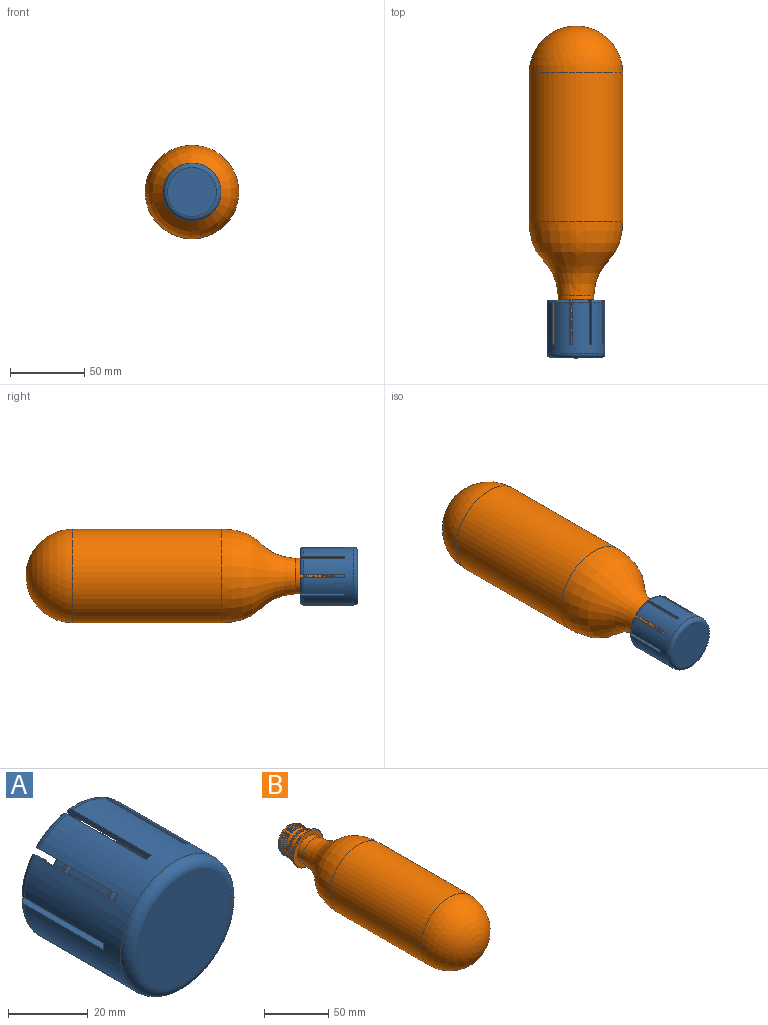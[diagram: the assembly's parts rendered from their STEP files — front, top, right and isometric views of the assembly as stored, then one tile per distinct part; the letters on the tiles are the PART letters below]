
ASSEMBLY  parts=2 mates=1
PART A: 105 faces, bbox 42.3x39.1x42.3 mm
  f0: cylinder r=17.5mm len=35mm, axis (0,-1,0), area 2702.5mm2, adj f1,f2,f3,f4,f5,f6,f7,f8
  f1: cone r=17.5mm half-angle=45deg, axis (0,-1,0), area 14mm2, adj f0,f10,f92,f103
  f2: cone r=17.5mm half-angle=45deg, axis (0,-1,0), area 14mm2, adj f0,f11,f95,f100
  f3: cone r=17.5mm half-angle=45deg, axis (0,-1,0), area 14mm2, adj f0,f12,f97,f101
  f4: cone r=17.5mm half-angle=45deg, axis (0,-1,0), area 14mm2, adj f0,f13,f80,f94
  f5: cone r=17.5mm half-angle=45deg, axis (0,-1,0), area 14mm2, adj f0,f14,f89,f91
  f6: cone r=17.5mm half-angle=45deg, axis (0,-1,0), area 14mm2, adj f0,f15,f86,f88
  f7: cone r=17.5mm half-angle=45deg, axis (0,-1,0), area 14mm2, adj f0,f16,f83,f85
  f8: cone r=17.5mm half-angle=45deg, axis (0,-1,0), area 14mm2, adj f0,f17,f82,f98
  f9: cone r=17.5mm half-angle=45deg, axis (0,-1,0), area 14mm2, adj f0,f18,f79,f104
  f10: plane 7.88x7.04mm, normal (0,-1,0), area 17.6mm2, adj f1,f19,f92,f103
  f11: plane 9.24x3.47mm, normal (0,-1,0), area 17.6mm2, adj f2,f20,f95,f100
  f12: plane 8.48x5.98mm, normal (0,-1,0), area 17.6mm2, adj f3,f21,f97,f101
  f13: plane 7.88x7.04mm, normal (0,-1,0), area 17.6mm2, adj f4,f22,f80,f94
  f14: plane 9.24x3.47mm, normal (0,-1,0), area 17.6mm2, adj f5,f23,f89,f91
  f15: plane 8.48x5.98mm, normal (0,-1,0), area 17.6mm2, adj f6,f24,f86,f88
  f16: plane 8.82x4.75mm, normal (0,-1,0), area 17.6mm2, adj f7,f25,f83,f85
  f17: plane 8.82x4.75mm, normal (0,-1,0), area 17.6mm2, adj f8,f26,f82,f98
  f18: plane 9.39x2.57mm, normal (0,-1,0), area 17.6mm2, adj f9,f27,f79,f104
  f19: cylinder r=14.5mm len=6.14mm, axis (0,-1,0), area 8.1mm2, adj f10,f28,f92,f103
  f20: cylinder r=14.5mm len=7.89mm, axis (0,-1,0), area 8.1mm2, adj f11,f29,f95,f100
  f21: cylinder r=14.5mm len=6.94mm, axis (0,-1,0), area 8.1mm2, adj f12,f30,f97,f101
  f22: cylinder r=14.5mm len=6.14mm, axis (0,-1,0), area 8.1mm2, adj f13,f31,f80,f94
  f23: cylinder r=14.5mm len=7.89mm, axis (0,-1,0), area 8.1mm2, adj f14,f32,f89,f91
  f24: cylinder r=14.5mm len=6.94mm, axis (0,-1,0), area 8.1mm2, adj f15,f33,f86,f88
  f25: cylinder r=14.5mm len=7.53mm, axis (0,-1,0), area 8.1mm2, adj f16,f34,f83,f85
  f26: cylinder r=14.5mm len=7.53mm, axis (0,-1,0), area 8.1mm2, adj f17,f35,f82,f98
  f27: cylinder r=14.5mm len=8.02mm, axis (0,-1,0), area 8.1mm2, adj f18,f36,f79,f104
  f28: cone r=14.5mm half-angle=45deg, axis (0,1,0), area 12mm2, adj f19,f37,f92,f103
  f29: cone r=14.5mm half-angle=45deg, axis (0,1,0), area 12mm2, adj f20,f38,f95,f100
  f30: cone r=14.5mm half-angle=45deg, axis (0,1,0), area 12mm2, adj f21,f39,f97,f101
  f31: cone r=14.5mm half-angle=45deg, axis (0,1,0), area 12mm2, adj f22,f40,f80,f94
  f32: cone r=14.5mm half-angle=45deg, axis (0,1,0), area 12mm2, adj f23,f41,f89,f91
  f33: cone r=14.5mm half-angle=45deg, axis (0,1,0), area 12mm2, adj f24,f42,f86,f88
  f34: cone r=14.5mm half-angle=45deg, axis (0,1,0), area 12mm2, adj f25,f43,f83,f85
  f35: cone r=14.5mm half-angle=45deg, axis (0,1,0), area 12mm2, adj f26,f44,f82,f98
  f36: cone r=14.5mm half-angle=45deg, axis (0,1,0), area 12mm2, adj f27,f45,f79,f104
  f37: plane 8.4x7.48mm, normal (0,1,0), area 19mm2, adj f28,f47,f92,f103
  f38: plane 9.92x3.6mm, normal (0,1,0), area 19mm2, adj f29,f48,f95,f100
  f39: plane 9.07x6.32mm, normal (0,1,0), area 19mm2, adj f30,f49,f97,f101
  f40: plane 8.4x7.48mm, normal (0,1,0), area 19mm2, adj f31,f50,f80,f94
  f41: plane 9.92x3.6mm, normal (0,1,0), area 19mm2, adj f32,f51,f89,f91
  f42: plane 9.07x6.32mm, normal (0,1,0), area 19mm2, adj f33,f52,f86,f88
  f43: plane 9.46x4.98mm, normal (0,1,0), area 19mm2, adj f34,f53,f83,f85
  f44: plane 9.46x4.98mm, normal (0,1,0), area 19mm2, adj f35,f54,f82,f98
  f45: plane 10.07x2.62mm, normal (0,1,0), area 19mm2, adj f36,f55,f79,f104
  f46: cylinder r=19.5mm len=39mm, axis (0,-1,0), area 3661.5mm2, adj f47,f48,f49,f50,f51,f52,f53,f54
  f47: torus R=17.5mm, axis (0,-1,0), area 34.8mm2, adj f37,f46,f92,f103
  f48: torus R=17.5mm, axis (0,-1,0), area 34.8mm2, adj f38,f46,f95,f100
  f49: torus R=17.5mm, axis (0,-1,0), area 34.8mm2, adj f39,f46,f97,f101
  f50: torus R=17.5mm, axis (0,-1,0), area 34.8mm2, adj f40,f46,f80,f94
  f51: torus R=17.5mm, axis (0,-1,0), area 34.8mm2, adj f41,f46,f89,f91
  f52: torus R=17.5mm, axis (0,-1,0), area 34.8mm2, adj f42,f46,f86,f88
  f53: torus R=17.5mm, axis (0,-1,0), area 34.8mm2, adj f43,f46,f83,f85
  f54: torus R=17.5mm, axis (0,-1,0), area 34.8mm2, adj f44,f46,f82,f98
  f55: torus R=17.5mm, axis (0,-1,0), area 34.8mm2, adj f45,f46,f79,f104
  f56: cylinder r=10.5mm len=21mm, axis (0,-1,0), area 712.5mm2, adj f58,f69
  f57: plane 33x33mm, normal (0,-1,0), area 855.3mm2, adj f76
  f58: plane 31x31mm, normal (0,1,0), area 408.4mm2, adj f56,f77
  f59: plane 20.6x20.6mm, normal (0,-1,0), area 34.6mm2, adj f61,f70
  f60: plane 20.6x20.6mm, normal (0,1,0), area 34.6mm2, adj f61,f69
  f61: torus R=9.75mm, axis (0,-1,0), area 179.9mm2, adj f59,f60
  f62: cylinder r=10.5mm len=21mm, axis (0,-1,0), area 897.2mm2, adj f70,f71
  f63: plane 20.6x20.6mm, normal (0,1,0), area 34.6mm2, adj f65,f71
  f64: plane 20.6x20.6mm, normal (0,-1,0), area 34.6mm2, adj f65,f72
  f65: torus R=9.75mm, axis (0,-1,0), area 179.9mm2, adj f63,f64
  f66: plane 19x19mm, normal (0,1,0), area 129.6mm2, adj f67,f73
  f67: cone r=9.5mm half-angle=45deg, axis (0,-1,0), area 88.9mm2, adj f66,f68
  f68: cylinder r=10.5mm len=21mm, axis (0,-1,0), area 184.7mm2, adj f67,f72
  f69: cone r=10.5mm half-angle=45deg, axis (0,-1,0), area 18.5mm2, adj f56,f60
  f70: cone r=10.5mm half-angle=45deg, axis (0,1,0), area 18.5mm2, adj f59,f62
  f71: cone r=10.3mm half-angle=45deg, axis (0,-1,0), area 18.5mm2, adj f62,f63
  f72: cone r=10.3mm half-angle=45deg, axis (0,1,0), area 18.5mm2, adj f64,f68
  f73: cylinder r=7mm len=25mm, axis (0,1,0), area 1099.6mm2, adj f66,f75
  f74: plane 4x4mm, normal (0,1,0), area 12.6mm2, adj f75
  f75: torus R=2mm, axis (0,1,0), area 255.8mm2, adj f73,f74
  f76: torus R=16.5mm, axis (0,1,0), area 545.1mm2, adj f46,f57
  f77: torus R=15.5mm, axis (0,-1,0), area 331.1mm2, adj f0,f58
  f78: plane 2.57x2.56mm, normal (0,1,0), area 4mm2, adj f0,f46,f79,f80
  f79: plane 30.05x4.76mm, normal (-0.34,0,0.94), area 65.2mm2, adj f0,f9,f18,f27,f36,f45,f46,f55
  f80: plane 30.05x4.76mm, normal (0.34,0,-0.94), area 65.2mm2, adj f0,f4,f13,f22,f31,f40,f46,f50
  f81: plane 2.03x2mm, normal (0,1,0), area 4mm2, adj f0,f46,f82,f83
  f82: plane 30.05x5.06mm, normal (0,0,-1), area 65.2mm2, adj f0,f8,f17,f26,f35,f44,f46,f54
  f83: plane 30.05x5.06mm, normal (0,0,1), area 65.2mm2, adj f0,f7,f16,f25,f34,f43,f46,f53
  f84: plane 2.82x2.82mm, normal (0,1,0), area 4mm2, adj f0,f46,f85,f86
  f85: plane 30.05x3.89mm, normal (0.64,0,-0.77), area 65.2mm2, adj f0,f7,f16,f25,f34,f43,f46,f53
  f86: plane 30.05x3.89mm, normal (-0.64,0,0.77), area 65.2mm2, adj f0,f6,f15,f24,f33,f42,f46,f52
  f87: plane 2.32x2.32mm, normal (0,1,0), area 4mm2, adj f0,f46,f88,f89
  f88: plane 30.05x4.98mm, normal (0.98,0,-0.17), area 65.2mm2, adj f0,f6,f15,f24,f33,f42,f46,f52
  f89: plane 30.05x4.98mm, normal (-0.98,0,0.17), area 65.2mm2, adj f0,f5,f14,f23,f32,f41,f46,f51
  f90: plane 2.73x2.73mm, normal (0,1,0), area 4mm2, adj f0,f46,f91,f92
  f91: plane 30.05x4.39mm, normal (0.87,0,0.5), area 65.2mm2, adj f0,f5,f14,f23,f32,f41,f46,f51
  f92: plane 30.05x4.39mm, normal (-0.87,0,-0.5), area 65.2mm2, adj f0,f1,f10,f19,f28,f37,f46,f47
  f93: plane 2.73x2.73mm, normal (0,1,0), area 4mm2, adj f0,f46,f94,f95
  f94: plane 30.05x4.39mm, normal (-0.87,0,0.5), area 65.2mm2, adj f0,f4,f13,f22,f31,f40,f46,f50
  f95: plane 30.05x4.39mm, normal (0.87,0,-0.5), area 65.2mm2, adj f0,f2,f11,f20,f29,f38,f46,f48
  f96: plane 2.82x2.82mm, normal (0,1,0), area 4mm2, adj f0,f46,f97,f98
  f97: plane 30.05x3.89mm, normal (-0.64,0,-0.77), area 65.2mm2, adj f0,f3,f12,f21,f30,f39,f46,f49
  f98: plane 30.05x3.89mm, normal (0.64,0,0.77), area 65.2mm2, adj f0,f8,f17,f26,f35,f44,f46,f54
  f99: plane 2.32x2.32mm, normal (0,1,0), area 4mm2, adj f0,f46,f100,f101
  f100: plane 30.05x4.98mm, normal (-0.98,0,-0.17), area 65.2mm2, adj f0,f2,f11,f20,f29,f38,f46,f48
  f101: plane 30.05x4.98mm, normal (0.98,0,0.17), area 65.2mm2, adj f0,f3,f12,f21,f30,f39,f46,f49
  f102: plane 2.57x2.56mm, normal (0,1,0), area 4mm2, adj f0,f46,f103,f104
  f103: plane 30.05x4.76mm, normal (0.34,0,0.94), area 65.2mm2, adj f0,f1,f10,f19,f28,f37,f46,f47
  f104: plane 30.05x4.76mm, normal (-0.34,0,-0.94), area 65.2mm2, adj f0,f9,f18,f27,f36,f45,f46,f55
PART B: 323 faces, bbox 63x207.7x63 mm
  f0: plane 22x22mm, normal (0,-1,0), area 16.1mm2, adj f284,f322
  f1: cylinder r=12.26mm len=24.51mm, axis (0,1,0), area 270.6mm2, adj f14,f199,f200,f215,f216,f217,f218,f219
  f2: bspline ~17.68x9.49mm, area 6.4mm2, adj f3,f24,f177,f207
  f3: bspline ~1.8x1.33mm, area 0.7mm2, adj f2,f29,f30,f208,f209,f293
  f4: cylinder r=16.5mm len=33mm, axis (0,-1,0), area 65.2mm2, adj f9,f17
  f5: plane 32.2x32.2mm, normal (0,-1,0), area 361.9mm2, adj f17,f318
  f6: torus R=14.36mm, axis (0,-1,0), area 154.3mm2, adj f7,f8
  f7: cone r=16.5mm half-angle=71deg, axis (0,-1,0), area 219mm2, adj f6,f9
  f8: cylinder r=12.86mm len=25.71mm, axis (0,-1,0), area 233.4mm2, adj f6,f15
  f9: torus R=15.86mm, axis (0,1,0), area 81.5mm2, adj f4,f7
  f10: cylinder r=13.98mm len=27.97mm, axis (0,-1,0), area 21.9mm2, adj f13,f16
  f11: plane 27.17x27.17mm, normal (0,-1,0), area 27.8mm2, adj f12,f15
  f12: cone r=13.98mm half-angle=89.5deg, axis (0,1,0), area 13.1mm2, adj f11,f16
  f13: torus R=12.19mm, axis (0,1,0), area 188.6mm2, adj f10,f14
  f14: torus R=13.06mm, axis (0,1,0), area 76.9mm2, adj f1,f13
  f15: torus R=13.25mm, axis (0,1,0), area 51.3mm2, adj f8,f11
  f16: torus R=13.74mm, axis (0,-1,0), area 34.1mm2, adj f10,f12
  f17: torus R=16.1mm, axis (0,1,0), area 64.6mm2, adj f4,f5
  f18: plane 23.78x23.78mm, normal (0,1,0), area 52.2mm2, adj f19,f285
  f19: torus R=11.89mm, axis (0,1,0), area 70.2mm2, adj f18,f20
  f20: cylinder r=12.47mm len=24.94mm, axis (0,1,0), area 32.9mm2, adj f19,f21
  f21: plane 25.07x25.07mm, normal (0,1,0), area 5.1mm2, adj f20,f22
  f22: cylinder r=12.54mm len=25.07mm, axis (0,1,0), area 26.9mm2, adj f21,f178,f197,f198,f201,f202,f204,f205
  f23: bspline ~24.84x8.59mm, area 3.5mm2, adj f24,f26,f31,f191
  f24: bspline ~22.43x6.24mm, area 14.9mm2, adj f2,f23,f30,f176,f192,f195
  f25: bspline ~25.64x9.84mm, area 19.2mm2, adj f26,f33,f189,f299
  f26: bspline ~22.43x6.19mm, area 18.9mm2, adj f23,f25,f32,f190
  f27: plane 0.82x0.55mm, normal (-0.56,0,-0.83), area 0.3mm2, adj f189,f190,f191,f196,f298
  f28: plane 10.27x4.99mm, normal (0,1,0), area 4.5mm2, adj f176,f177,f196,f205
  f29: plane 0.71x0.67mm, normal (-0.56,0,0.83), area 0.3mm2, adj f3,f31,f33,f295
  f30: sphere r=0.64mm, area 0.6mm2, adj f3,f24,f31
  f31: bspline ~0.77x0.5mm, area 0.1mm2, adj f23,f29,f30,f32
  f32: sphere r=0.64mm, area 0.4mm2, adj f26,f31,f33
  f33: bspline ~2.32x1.7mm, area 0.8mm2, adj f25,f29,f32,f297
  f34: bspline ~12.87x9.55mm, area 7.6mm2, adj f36,f38,f45,f231
  f35: bspline ~12.01x6.95mm, area 1.7mm2, adj f36,f39,f41,f47
  f36: bspline ~11.69x5.81mm, area 9.4mm2, adj f34,f35,f43,f46
  f37: bspline ~12.81x9.65mm, area 7.6mm2, adj f40,f41,f49,f239
  f38: bspline ~5.65x4.41mm, area 1.2mm2, adj f34,f43,f232
  f39: bspline ~6.34x4.79mm, area 0.8mm2, adj f35,f42,f43,f236
  f40: bspline ~5.7x4.31mm, area 1.2mm2, adj f37,f42,f240
  f41: bspline ~11.67x5.85mm, area 9.4mm2, adj f35,f37,f42,f48
  f42: bspline ~6.09x3.8mm, area 3.8mm2, adj f39,f40,f41,f238
  f43: bspline ~5.63x3.35mm, area 3.7mm2, adj f36,f38,f39,f234
  f44: plane 0.6x0.54mm, normal (-0.56,0,-0.83), area 0.2mm2, adj f45,f47,f49,f235
  f45: bspline ~2.31x1.7mm, area 0.7mm2, adj f34,f44,f46,f233
  f46: sphere r=0.64mm, area 0.4mm2, adj f36,f45,f47
  f47: bspline ~0.76x0.72mm, area 0.1mm2, adj f35,f44,f46,f48
  f48: sphere r=0.64mm, area 0.3mm2, adj f41,f47,f49
  f49: bspline ~2.3x1.67mm, area 0.6mm2, adj f37,f44,f48,f237
  f50: plane 0.6x0.54mm, normal (-0.56,0,-0.83), area 0.2mm2, adj f57,f59,f61,f225
  f51: bspline ~22.41x6.3mm, area 18.7mm2, adj f54,f55,f58,f65
  f52: bspline ~22.41x6.34mm, area 18.7mm2, adj f53,f55,f60,f63
  f53: bspline ~24.86x8.99mm, area 15.2mm2, adj f52,f61,f62,f229
  f54: bspline ~24.86x8.89mm, area 15.2mm2, adj f51,f57,f66,f224
  f55: bspline ~24.87x7.99mm, area 3.5mm2, adj f51,f52,f59,f64
  f56: plane 0.6x0.54mm, normal (-0.56,0,0.83), area 0.2mm2, adj f62,f64,f66,f228
  f57: bspline ~2.31x1.7mm, area 0.7mm2, adj f50,f54,f58,f223
  f58: sphere r=0.64mm, area 0.4mm2, adj f51,f57,f59
  f59: bspline ~0.76x0.72mm, area 0.1mm2, adj f50,f55,f58,f60
  f60: sphere r=0.64mm, area 0.4mm2, adj f52,f59,f61
  f61: bspline ~2.3x1.67mm, area 0.6mm2, adj f50,f53,f60,f227
  f62: bspline ~2.32x1.7mm, area 0.7mm2, adj f53,f56,f63,f230
  f63: sphere r=0.64mm, area 0.5mm2, adj f52,f62,f64
  f64: bspline ~0.76x0.72mm, area 0.1mm2, adj f55,f56,f63,f65
  f65: sphere r=0.64mm, area 0.4mm2, adj f51,f64,f66
  f66: bspline ~2.29x1.66mm, area 0.6mm2, adj f54,f56,f65,f226
  f67: bspline ~11.24x1.74mm, area 6.6mm2, adj f68,f70,f77,f82
  f68: bspline ~13.15x4.07mm, area 5.5mm2, adj f67,f78,f83,f217
  f69: bspline ~11.24x1.71mm, area 6.6mm2, adj f70,f71,f75,f80
  f70: bspline ~11.38x1.47mm, area 1.2mm2, adj f67,f69,f76,f81
  f71: bspline ~13.15x4.01mm, area 5.5mm2, adj f69,f74,f79,f220
  f72: plane 0.74x0.65mm, normal (1,0,-0.03), area 0.3mm2, adj f74,f76,f78,f221
  f73: plane 0.74x0.65mm, normal (-1,0,-0.03), area 0.3mm2, adj f79,f81,f83,f216
  f74: bspline ~2.37x1.32mm, area 0.7mm2, adj f71,f72,f75,f222
  f75: sphere r=0.64mm, area 0.3mm2, adj f69,f74,f76
  f76: bspline ~0.59x0.5mm, area 0.1mm2, adj f70,f72,f75,f77
  f77: sphere r=0.64mm, area 0.4mm2, adj f67,f76,f78
  f78: bspline ~2.37x1.37mm, area 0.7mm2, adj f68,f72,f77,f219
  f79: bspline ~2.37x1.37mm, area 0.7mm2, adj f71,f73,f80,f218
  f80: sphere r=0.64mm, area 0.3mm2, adj f69,f79,f81
  f81: bspline ~0.59x0.5mm, area 0.1mm2, adj f70,f73,f80,f82
  f82: sphere r=0.64mm, area 0.3mm2, adj f67,f81,f83
  f83: bspline ~2.37x1.32mm, area 0.7mm2, adj f68,f73,f82,f215
  f84: bspline ~5.66x3.22mm, area 3.2mm2, adj f85,f86,f179,f305
  f85: bspline ~4.56x3.56mm, area 1.6mm2, adj f84,f87,f306
  f86: bspline ~6.72x1.64mm, area 3.5mm2, adj f84,f87,f89,f180,f184
  f87: bspline ~6.62x3.63mm, area 3.7mm2, adj f85,f86,f182,f307
  f88: plane 7.97x1.4mm, normal (0,1,0), area 4.7mm2, adj f179,f180,f181,f188,f212
  f89: bspline ~6.63x1.64mm, area 0.3mm2, adj f86,f181,f183,f185
  f90: plane 1x0.38mm, normal (1,0,-0.03), area 0.2mm2, adj f182,f184,f188,f309
  f91: plane 0.6x0.54mm, normal (0.56,0,-0.83), area 0.2mm2, adj f98,f100,f102,f254
  f92: bspline ~22.64x6.84mm, area 18.7mm2, adj f95,f96,f99,f104
  f93: bspline ~22.64x6.79mm, area 18.7mm2, adj f94,f96,f101,f106
  f94: bspline ~24.84x9.32mm, area 15.2mm2, adj f93,f102,f107,f255
  f95: bspline ~24.84x9.22mm, area 15.2mm2, adj f92,f98,f103,f250
  f96: bspline ~24.86x8.39mm, area 3.5mm2, adj f92,f93,f100,f105
  f97: plane 0.6x0.54mm, normal (0.56,0,0.83), area 0.2mm2, adj f103,f105,f107,f251
  f98: bspline ~2.29x1.66mm, area 0.6mm2, adj f91,f95,f99,f252
  f99: sphere r=0.64mm, area 0.6mm2, adj f92,f98,f100
  f100: bspline ~0.76x0.5mm, area 0.1mm2, adj f91,f96,f99,f101
  f101: sphere r=0.64mm, area 0.5mm2, adj f93,f100,f102
  f102: bspline ~1.83x1.37mm, area 0.7mm2, adj f91,f94,f101,f256
  f103: bspline ~2.31x1.7mm, area 0.7mm2, adj f95,f97,f104,f249
  f104: sphere r=0.64mm, area 0.5mm2, adj f92,f103,f105
  f105: bspline ~0.76x0.5mm, area 0.1mm2, adj f96,f97,f104,f106
  f106: sphere r=0.64mm, area 0.4mm2, adj f93,f105,f107
  f107: bspline ~2.3x1.67mm, area 0.6mm2, adj f94,f97,f106,f253
  f108: plane 0.6x0.54mm, normal (0.56,0,-0.83), area 0.2mm2, adj f115,f117,f119,f270
  f109: bspline ~22.43x6.07mm, area 18.7mm2, adj f112,f113,f116,f121
  f110: bspline ~22.43x6.11mm, area 18.7mm2, adj f111,f113,f118,f123
  f111: bspline ~25.34x9.39mm, area 15.2mm2, adj f110,f119,f124,f271
  f112: bspline ~25.34x9.28mm, area 15.2mm2, adj f109,f115,f120,f266
  f113: bspline ~25.36x8.47mm, area 3.5mm2, adj f109,f110,f117,f122
  f114: plane 0.6x0.54mm, normal (0.56,0,0.83), area 0.2mm2, adj f120,f122,f124,f267
  f115: bspline ~2.29x1.66mm, area 0.6mm2, adj f108,f112,f116,f268
  f116: sphere r=0.64mm, area 0.6mm2, adj f109,f115,f117
  f117: bspline ~0.76x0.5mm, area 0.1mm2, adj f108,f113,f116,f118
  f118: sphere r=0.64mm, area 0.5mm2, adj f110,f117,f119
  f119: bspline ~2.32x1.7mm, area 0.7mm2, adj f108,f111,f118,f272
  f120: bspline ~2.31x1.7mm, area 0.7mm2, adj f112,f114,f121,f265
  f121: sphere r=0.64mm, area 0.4mm2, adj f109,f120,f122
  f122: bspline ~0.76x0.72mm, area 0.1mm2, adj f113,f114,f121,f123
  f123: sphere r=0.64mm, area 0.4mm2, adj f110,f122,f124
  f124: bspline ~2.3x1.67mm, area 0.6mm2, adj f111,f114,f123,f269
  f125: bspline ~13.2x1.99mm, area 1.2mm2, adj f127,f129,f134,f139
  f126: bspline ~13.16x3.98mm, area 5.5mm2, adj f127,f132,f137,f258
  f127: bspline ~9.82x1.35mm, area 6.6mm2, adj f125,f126,f133,f138
  f128: bspline ~13.16x3.92mm, area 5.5mm2, adj f129,f136,f141,f263
  f129: bspline ~9.82x1.32mm, area 6.6mm2, adj f125,f128,f135,f140
  f130: plane 0.74x0.65mm, normal (1,0,0.03), area 0.3mm2, adj f137,f139,f141,f259
  f131: plane 0.74x0.65mm, normal (-1,0,0.03), area 0.3mm2, adj f132,f134,f136,f262
  f132: bspline ~2.37x1.32mm, area 0.7mm2, adj f126,f131,f133,f260
  f133: sphere r=0.64mm, area 0.3mm2, adj f127,f132,f134
  f134: bspline ~0.59x0.5mm, area 0.1mm2, adj f125,f131,f133,f135
  f135: sphere r=0.64mm, area 0.3mm2, adj f129,f134,f136
  f136: bspline ~2.37x1.37mm, area 0.7mm2, adj f128,f131,f135,f264
  f137: bspline ~2.37x1.37mm, area 0.7mm2, adj f126,f130,f138,f257
  f138: sphere r=0.64mm, area 0.4mm2, adj f127,f137,f139
  f139: bspline ~0.59x0.5mm, area 0.1mm2, adj f125,f130,f138,f140
  f140: sphere r=0.64mm, area 0.3mm2, adj f129,f139,f141
  f141: bspline ~2.37x1.32mm, area 0.7mm2, adj f128,f130,f140,f261
  f142: plane 0.74x0.65mm, normal (1,0,0.03), area 0.3mm2, adj f154,f156,f158,f277
  f143: bspline ~14.75x4.27mm, area 5.9mm2, adj f147,f149,f154,f274,f276
  f144: bspline ~14.75x4.21mm, area 5.5mm2, adj f146,f153,f158,f281
  f145: bspline ~14.78x2.33mm, area 1.2mm2, adj f146,f147,f151,f156
  f146: bspline ~11.25x1.67mm, area 6.6mm2, adj f144,f145,f152,f157
  f147: bspline ~11.25x1.69mm, area 6.6mm2, adj f143,f145,f150,f155
  f148: plane 0.74x0.65mm, normal (-1,0,0.03), area 0.3mm2, adj f149,f151,f153,f280
  f149: bspline ~2.37x1.32mm, area 0.7mm2, adj f143,f148,f150,f278
  f150: sphere r=0.64mm, area 0.3mm2, adj f147,f149,f151
  f151: bspline ~0.59x0.5mm, area 0.1mm2, adj f145,f148,f150,f152
  f152: sphere r=0.64mm, area 0.3mm2, adj f146,f151,f153
  f153: bspline ~2.37x1.37mm, area 0.7mm2, adj f144,f148,f152,f282
  f154: bspline ~2.37x1.37mm, area 0.8mm2, adj f142,f143,f155,f273,f275
  f155: sphere r=0.64mm, area 0.4mm2, adj f147,f154,f156
  f156: bspline ~0.59x0.5mm, area 0.1mm2, adj f142,f145,f155,f157
  f157: sphere r=0.64mm, area 0.3mm2, adj f146,f156,f158
  f158: bspline ~2.37x1.32mm, area 0.7mm2, adj f142,f144,f157,f279
  f159: bspline ~11.22x1.98mm, area 6.6mm2, adj f160,f162,f169,f174
  f160: bspline ~13.17x3.73mm, area 5.5mm2, adj f159,f170,f175,f247
  f161: bspline ~11.22x1.95mm, area 6.6mm2, adj f162,f163,f167,f172
  f162: bspline ~13.21x1.76mm, area 1.2mm2, adj f159,f161,f168,f173
  f163: bspline ~13.17x3.78mm, area 5.5mm2, adj f161,f166,f171,f242
  f164: plane 0.74x0.65mm, normal (1,0,-0.03), area 0.3mm2, adj f166,f168,f170,f246
  f165: plane 0.74x0.65mm, normal (-1,0,-0.03), area 0.3mm2, adj f171,f173,f175,f243
  f166: bspline ~2.37x1.32mm, area 0.7mm2, adj f163,f164,f167,f244
  f167: sphere r=0.64mm, area 0.3mm2, adj f161,f166,f168
  f168: bspline ~0.59x0.5mm, area 0.1mm2, adj f162,f164,f167,f169
  f169: sphere r=0.64mm, area 0.4mm2, adj f159,f168,f170
  f170: bspline ~2.37x1.37mm, area 0.7mm2, adj f160,f164,f169,f248
  f171: bspline ~2.37x1.37mm, area 0.7mm2, adj f163,f165,f172,f241
  f172: sphere r=0.64mm, area 0.3mm2, adj f161,f171,f173
  f173: bspline ~0.59x0.5mm, area 0.1mm2, adj f162,f165,f172,f174
  f174: sphere r=0.64mm, area 0.3mm2, adj f159,f173,f175
  f175: bspline ~2.37x1.32mm, area 0.7mm2, adj f160,f165,f174,f245
  f176: bspline ~8.35x4.97mm, area 2.3mm2, adj f24,f28,f177,f195
  f177: bspline ~8.74x0.85mm, area 0.3mm2, adj f2,f28,f176,f206
  f178: cylinder r=0.4mm len=0.96mm, axis (0,1,0), area 0.1mm2, adj f22,f209,f286,f289
  f179: bspline ~6.37x3.38mm, area 0.9mm2, adj f84,f88,f180,f213,f214,f302,f303,f304
  f180: bspline ~1.62x0.19mm, area 0.1mm2, adj f86,f88,f179,f181
  f181: bspline ~4.5x0.97mm, area 0.6mm2, adj f88,f89,f180,f185
  f182: bspline ~2.28x1.14mm, area 0.5mm2, adj f87,f90,f184,f308
  f183: bspline ~0.37x0.27mm, area 0mm2, adj f89,f184,f186
  f184: bspline ~0.75x0.55mm, area 0.3mm2, adj f86,f90,f182,f183,f187
  f185: bspline ~0.27x0.16mm, area 0mm2, adj f89,f181,f186,f188
  f186: bspline ~0.29x0.28mm, area 0mm2, adj f183,f185,f187,f188
  f187: bspline ~0.34x0.28mm, area 0mm2, adj f184,f186,f188
  f188: cylinder r=0.4mm len=1.4mm, axis (-0.03,0,-1), area 0.6mm2, adj f88,f90,f185,f186,f187,f210,f211,f310
  f189: bspline ~2.1x1.49mm, area 0.5mm2, adj f25,f27,f190,f300
  f190: bspline ~0.67x0.66mm, area 0.3mm2, adj f26,f27,f189,f191
  f191: bspline ~0.5x0.47mm, area 0mm2, adj f23,f27,f190,f192,f193
  f192: bspline ~0.48x0.22mm, area 0mm2, adj f24,f191,f194
  f193: bspline ~0.45x0.37mm, area 0mm2, adj f191,f194,f196
  f194: bspline ~0.33x0.29mm, area 0mm2, adj f192,f193,f195,f196
  f195: bspline ~0.33x0.3mm, area 0mm2, adj f24,f176,f194,f196
  f196: cylinder r=0.4mm len=1.17mm, axis (-0.83,0,0.56), area 0.5mm2, adj f27,f28,f193,f194,f195,f203,f204,f292
  f197: cylinder r=0.4mm len=0.08mm, axis (0,1,0), area 0mm2, adj f22,f210,f314
  f198: cylinder r=0.4mm len=0.04mm, axis (0,1,0), area 0mm2, adj f22,f203,f288
  f199: torus R=12.65mm, axis (0,1,0), area 14mm2, adj f1,f201,f273,f274,f287,f303
  f200: torus R=12.65mm, axis (0,1,0), area 0.8mm2, adj f1,f202,f294,f311
  f201: torus R=12.13mm, axis (0,-1,0), area 14.6mm2, adj f22,f199,f286,f301,f302
  f202: torus R=12.13mm, axis (0,-1,0), area 1mm2, adj f22,f200,f288,f292,f312,f313,f314
  f203: bspline ~0.41x0.37mm, area 0mm2, adj f196,f198,f204,f290
  f204: bspline ~0.62x0.46mm, area 0.1mm2, adj f22,f196,f203,f205
  f205: torus R=12.94mm, axis (0,1,0), area 7.1mm2, adj f22,f28,f204,f206
  f206: bspline ~2.68x0.56mm, area 1.1mm2, adj f22,f177,f205,f207
  f207: bspline ~10.43x6.12mm, area 4.6mm2, adj f2,f22,f206,f208
  f208: bspline ~0.65x0.48mm, area 0.1mm2, adj f3,f22,f207,f209
  f209: bspline ~0.74x0.71mm, area 0.2mm2, adj f3,f178,f208,f291
  f210: bspline ~0.45x0.44mm, area 0mm2, adj f188,f197,f211,f313
  f211: bspline ~0.57x0.53mm, area 0.1mm2, adj f22,f188,f210,f212
  f212: torus R=12.93mm, axis (0,1,0), area 5mm2, adj f22,f88,f211,f213
  f213: bspline ~1.31x0.93mm, area 0.2mm2, adj f22,f179,f212,f214
  f214: bspline ~0.54x0.53mm, area 0.1mm2, adj f179,f213,f301
  f215: bspline ~1.5x1.34mm, area 0.9mm2, adj f1,f83,f216,f217
  f216: cylinder r=0.64mm len=0.65mm, axis (0,1,0), area 0.5mm2, adj f1,f73,f215,f218
  f217: bspline ~9.87x1.59mm, area 6.4mm2, adj f1,f68,f215,f219
  f218: bspline ~1.5x1.43mm, area 1mm2, adj f1,f79,f216,f220
  f219: bspline ~1.5x1.43mm, area 1mm2, adj f1,f78,f217,f221
  f220: bspline ~10.86x1.62mm, area 6.4mm2, adj f1,f71,f218,f222
  f221: cylinder r=0.64mm len=0.65mm, axis (0,1,0), area 0.5mm2, adj f1,f72,f219,f222
  f222: bspline ~1.5x1.34mm, area 0.9mm2, adj f1,f74,f220,f221
  f223: bspline ~1.53x1.38mm, area 1mm2, adj f1,f57,f224,f225
  f224: bspline ~20.86x6.13mm, area 17.4mm2, adj f1,f54,f223,f226
  f225: cylinder r=0.64mm len=0.71mm, axis (0,1,0), area 0.4mm2, adj f1,f50,f223,f227
  f226: bspline ~1.53x1.34mm, area 1mm2, adj f1,f66,f224,f228
  f227: bspline ~1.53x1.34mm, area 1mm2, adj f1,f61,f225,f229
  f228: cylinder r=0.64mm len=0.71mm, axis (0,1,0), area 0.4mm2, adj f1,f56,f226,f230
  f229: bspline ~21.47x6.19mm, area 17.4mm2, adj f1,f53,f227,f230
  f230: bspline ~1.53x1.38mm, area 1mm2, adj f1,f62,f228,f229
  f231: bspline ~12.13x6.12mm, area 8.7mm2, adj f1,f34,f232,f233
  f232: bspline ~6.08x1.34mm, area 2.7mm2, adj f1,f38,f231,f234
  f233: bspline ~1.53x1.38mm, area 1mm2, adj f1,f45,f231,f235
  f234: bspline ~2.75x1.49mm, area 1.3mm2, adj f1,f43,f232,f236
  f235: cylinder r=0.64mm len=0.71mm, axis (0,1,0), area 0.4mm2, adj f1,f44,f233,f237
  f236: bspline ~0.5x0.23mm, area 0mm2, adj f1,f39,f234,f238
  f237: bspline ~1.53x1.34mm, area 1mm2, adj f1,f49,f235,f239
  f238: bspline ~3.53x1.72mm, area 1.2mm2, adj f1,f42,f236,f240
  f239: bspline ~12.08x6.19mm, area 8.7mm2, adj f1,f37,f237,f240
  f240: bspline ~6.53x1mm, area 2.7mm2, adj f1,f40,f238,f239
  f241: bspline ~1.5x1.43mm, area 1mm2, adj f1,f171,f242,f243
  f242: bspline ~10.86x1.62mm, area 6.4mm2, adj f1,f163,f241,f244
  f243: cylinder r=0.64mm len=0.65mm, axis (0,1,0), area 0.5mm2, adj f1,f165,f241,f245
  f244: bspline ~1.5x1.34mm, area 0.9mm2, adj f1,f166,f242,f246
  f245: bspline ~1.5x1.34mm, area 0.9mm2, adj f1,f175,f243,f247
  f246: cylinder r=0.64mm len=0.65mm, axis (0,1,0), area 0.5mm2, adj f1,f164,f244,f248
  f247: bspline ~10.86x1.62mm, area 6.4mm2, adj f1,f160,f245,f248
  f248: bspline ~1.5x1.43mm, area 1mm2, adj f1,f170,f246,f247
  f249: bspline ~1.53x1.38mm, area 1mm2, adj f1,f103,f250,f251
  f250: bspline ~20.86x6.13mm, area 17.4mm2, adj f1,f95,f249,f252
  f251: cylinder r=0.64mm len=0.71mm, axis (0,1,0), area 0.4mm2, adj f1,f97,f249,f253
  f252: bspline ~1.53x1.34mm, area 1mm2, adj f1,f98,f250,f254
  f253: bspline ~1.53x1.34mm, area 1mm2, adj f1,f107,f251,f255
  f254: cylinder r=0.64mm len=0.71mm, axis (0,1,0), area 0.4mm2, adj f1,f91,f252,f256
  f255: bspline ~21.47x6.19mm, area 17.4mm2, adj f1,f94,f253,f256
  f256: bspline ~1.53x1.38mm, area 1mm2, adj f1,f102,f254,f255
  f257: bspline ~1.5x1.43mm, area 1mm2, adj f1,f137,f258,f259
  f258: bspline ~10.86x1.62mm, area 6.4mm2, adj f1,f126,f257,f260
  f259: cylinder r=0.64mm len=0.65mm, axis (0,1,0), area 0.5mm2, adj f1,f130,f257,f261
  f260: bspline ~1.34x1.26mm, area 0.9mm2, adj f1,f132,f258,f262
  f261: bspline ~1.5x1.34mm, area 0.9mm2, adj f1,f141,f259,f263
  f262: cylinder r=0.64mm len=0.65mm, axis (0,1,0), area 0.5mm2, adj f1,f131,f260,f264
  f263: bspline ~10.86x1.62mm, area 6.4mm2, adj f1,f128,f261,f264
  f264: bspline ~1.5x1.43mm, area 1mm2, adj f1,f136,f262,f263
  f265: bspline ~1.53x1.38mm, area 1mm2, adj f1,f120,f266,f267
  f266: bspline ~21.46x6.19mm, area 17.4mm2, adj f1,f112,f265,f268
  f267: cylinder r=0.64mm len=0.71mm, axis (0,1,0), area 0.4mm2, adj f1,f114,f265,f269
  f268: bspline ~1.53x1.34mm, area 1mm2, adj f1,f115,f266,f270
  f269: bspline ~1.53x1.34mm, area 1mm2, adj f1,f124,f267,f271
  f270: cylinder r=0.64mm len=0.71mm, axis (0,1,0), area 0.4mm2, adj f1,f108,f268,f272
  f271: bspline ~21.46x6.19mm, area 17.4mm2, adj f1,f111,f269,f272
  f272: bspline ~1.53x1.38mm, area 1mm2, adj f1,f119,f270,f271
  f273: bspline ~0.76x0.59mm, area 0.3mm2, adj f154,f199,f274,f275
  f274: bspline ~9.89x1.52mm, area 4.6mm2, adj f143,f199,f273,f276
  f275: bspline ~1.29x0.63mm, area 0.5mm2, adj f1,f154,f273,f277
  f276: bspline ~2.79x1.32mm, area 0.6mm2, adj f1,f143,f274,f278
  f277: cylinder r=0.64mm len=0.65mm, axis (0,1,0), area 0.5mm2, adj f1,f142,f275,f279
  f278: bspline ~1.5x1.34mm, area 0.9mm2, adj f1,f149,f276,f280
  f279: bspline ~1.5x1.34mm, area 0.9mm2, adj f1,f158,f277,f281
  f280: cylinder r=0.64mm len=0.65mm, axis (0,1,0), area 0.5mm2, adj f1,f148,f278,f282
  f281: bspline ~10.86x1.62mm, area 6.4mm2, adj f1,f144,f279,f282
  f282: bspline ~1.5x1.43mm, area 1mm2, adj f1,f153,f280,f281
  f283: cylinder r=10.87mm len=21.74mm, axis (0,1,0), area 47.8mm2, adj f284,f285
  f284: cone r=10.87mm half-angle=0.3deg, axis (0,1,0), area 1372.9mm2, adj f0,f283
  f285: torus R=11.17mm, axis (0,1,0), area 32.5mm2, adj f18,f283
  f286: bspline ~0.69x0.69mm, area 0.1mm2, adj f178,f201,f287
  f287: sphere r=0.4mm, area 0.1mm2, adj f199,f286,f289
  f288: bspline ~0.24x0.21mm, area 0mm2, adj f198,f202,f290
  f289: cylinder r=0.4mm len=0.35mm, axis (0,1,0), area 0.1mm2, adj f1,f178,f287,f291
  f290: sphere r=0.4mm, area 0mm2, adj f203,f288,f292
  f291: sphere r=0.4mm, area 0mm2, adj f209,f289,f293
  f292: bspline ~1.09x0.75mm, area 0.3mm2, adj f196,f202,f290,f294
  f293: bspline ~0.64x0.49mm, area 0.1mm2, adj f1,f3,f291,f295
  f294: sphere r=0.4mm, area 0.1mm2, adj f200,f292,f296
  f295: cylinder r=0.4mm len=0.71mm, axis (0,1,0), area 0.3mm2, adj f1,f29,f293,f297
  f296: bspline ~0.47x0.36mm, area 0.1mm2, adj f1,f196,f294,f298
  f297: bspline ~1.11x1.05mm, area 0.6mm2, adj f1,f33,f295,f299
  f298: cylinder r=0.4mm len=0.51mm, axis (0,1,0), area 0.2mm2, adj f1,f27,f296,f300
  f299: bspline ~21.37x6.25mm, area 11mm2, adj f1,f25,f297,f300
  f300: bspline ~0.85x0.8mm, area 0.4mm2, adj f1,f189,f298,f299
  f301: bspline ~0.39x0.24mm, area 0.1mm2, adj f201,f214,f302
  f302: bspline ~1.42x1.15mm, area 0.4mm2, adj f179,f201,f301,f303
  f303: bspline ~0.36x0.2mm, area 0mm2, adj f179,f199,f302,f304
  f304: bspline ~0.21x0.2mm, area 0mm2, adj f1,f179,f303,f305
  f305: bspline ~2.68x1.31mm, area 0.5mm2, adj f1,f84,f304,f306
  f306: bspline ~5.95x1.16mm, area 1.9mm2, adj f1,f85,f305,f307
  f307: bspline ~8.31x1.55mm, area 2.1mm2, adj f1,f87,f306,f308
  f308: bspline ~0.92x0.75mm, area 0.4mm2, adj f1,f182,f307,f309
  f309: cylinder r=0.39mm len=0.38mm, axis (0,1,0), area 0.2mm2, adj f1,f90,f308,f310
  f310: bspline ~0.36x0.34mm, area 0.1mm2, adj f1,f188,f309,f311
  f311: bspline ~0.42x0.37mm, area 0.1mm2, adj f188,f200,f310,f312
  f312: bspline ~0.8x0.7mm, area 0.3mm2, adj f188,f202,f311,f313
  f313: bspline ~0.43x0.39mm, area 0mm2, adj f202,f210,f312,f314
  f314: bspline ~0.24x0.22mm, area 0mm2, adj f197,f202,f313
  f315: sphere r=31.5mm, area 6234.5mm2, adj f316
  f316: cylinder r=31.5mm len=100mm, axis (0,-1,0), area 19792mm2, adj f315,f317
  f317: revolved ~63x63mm, area 7735.1mm2, adj f316,f318
  f318: cylinder r=12mm len=24mm, axis (0,-1,0), area 377mm2, adj f5,f317
  f319: sphere r=30.5mm, area 5844.9mm2, adj f320
  f320: cylinder r=30.5mm len=100mm, axis (0,-1,0), area 19163mm2, adj f319,f321
  f321: revolved ~61x61mm, area 7359.3mm2, adj f320,f322
  f322: cylinder r=11mm len=22mm, axis (0,-1,0), area 345.7mm2, adj f0,f321
PLACE A t=(19.26,35.64,9.89)mm
PLACE B rot(axis=(1,0,0),180deg) t=(19.26,51.44,9.89)mm
MATE revolute A.f0 <-> B.f1  axis (0,-1,0) through (19.26,72.64,9.89)mm
